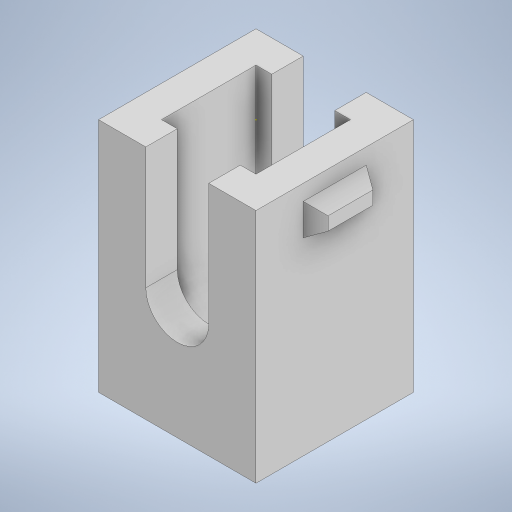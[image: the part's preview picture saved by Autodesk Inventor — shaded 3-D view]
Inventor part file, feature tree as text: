
AUTODESK INVENTOR PART (.ipt)
format: ipt  version: 2023 (Build 270158000, 158)  size: 243,712 bytes
history: native  units: in
note: dims shown in document units (in); Inventor stores cm internally (conversion verified against a paired STEP export)
features: sketch x9, extrude x4, shell x1
ambient origin geometry x8: Origin, YZ Plane, XZ Plane, XY Plane, X Axis, Y Axis, Z Axis, Center Point
bodies: Solid1 (feature_tree)
feature tree (14):
  extrude  "Extrusion1"  Depth=0.1969in
  shell  "Shell1"  Thickness=0.2953in
  sketch  "Sketch4"  dims[d4=0.0394in d10=0.0394in]
  sketch  "Sketch5"  dims[d11=0.0197in d12=-0.2061in d13=0.0394in]
  sketch  "Sketch6"  dims[d14=0.0787in d15=0.0394in]
  sketch  "Sketch7"  dims[d16=0.0787in]
  sketch  "Sketch8"  dims[d17=0.0394in]
  extrude  "Extrusion4"  Depth=0.0394in
  extrude  "Extrusion5"  Depth=0.0394in
  extrude  "Extrusion6"  Depth=0.0394in
  sketch  "Sketch1"  dims[d0=0.1969in d1=0.1969in d2=0.2953in d3=0.0in]
  sketch  "Sketch9"  dims[d18=0.0197in d19=-0.2061in]
  sketch  "Sketch10"  dims[d20=0.0787in]
  sketch  "Sketch11"  dims[d21=0.0in d22=0.0in]
